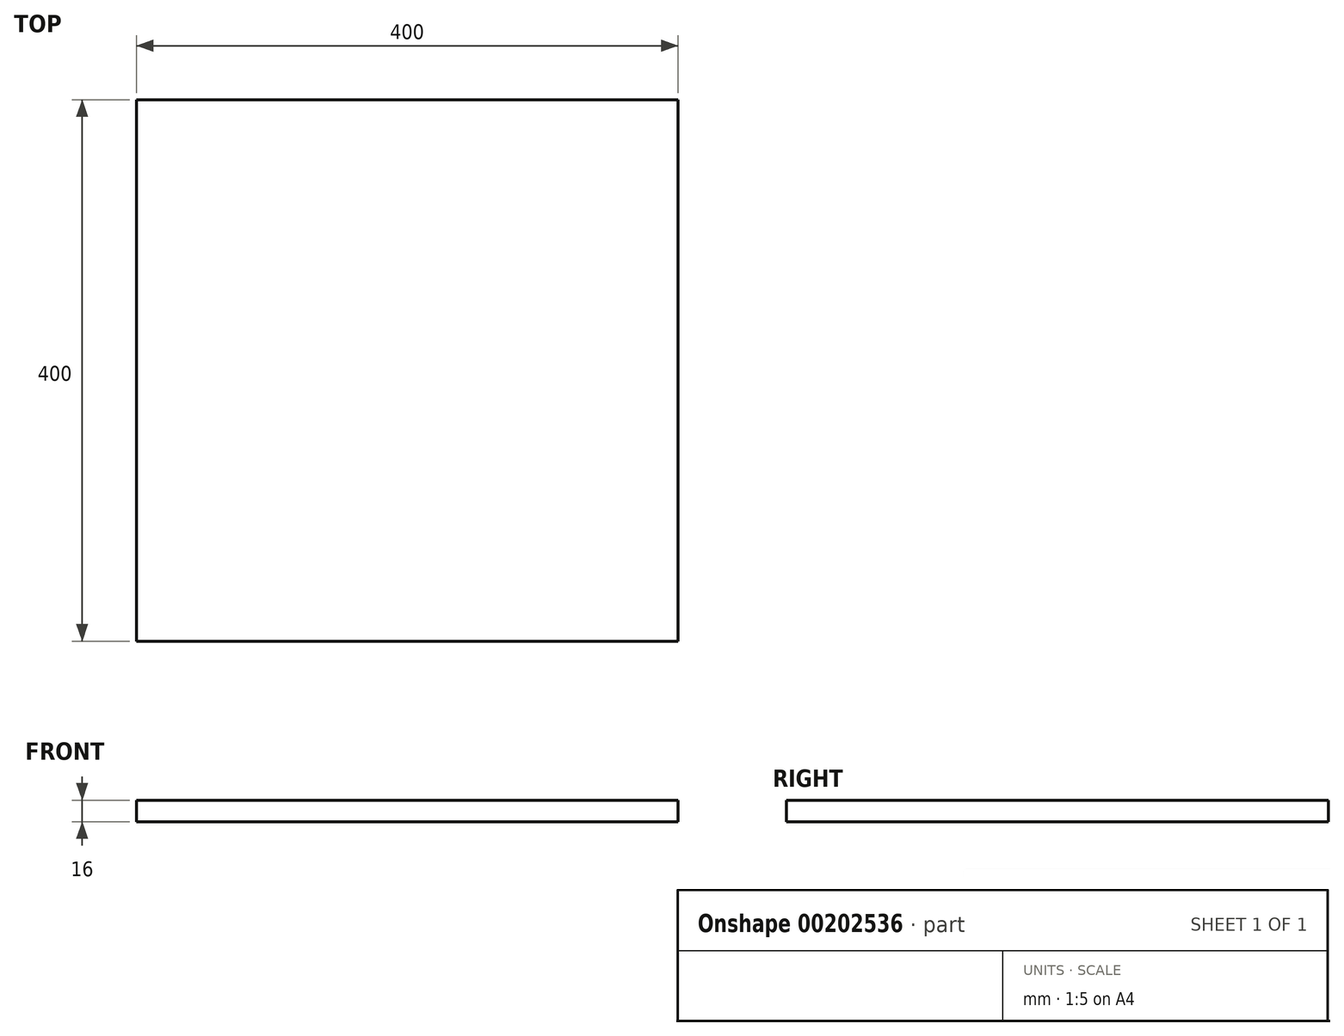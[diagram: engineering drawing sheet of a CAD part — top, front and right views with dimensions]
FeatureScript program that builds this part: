
annotation { "Feature Type Name" : "Feature", "Feature Type Description" : "" }
export const myFeature = defineFeature(function(context is Context, id is Id, definition is map)
    precondition{}
    {
        {
            var Q0;
            Q0=qCreatedBy(makeId("Top.planeOp"),FACE);
            var sketch = newSketch(context, id + "F0", { "sketchPlane" : qUnion([Q0])});
            skLineSegment(sketch, "E0.bottom", {"start": v(-276.3, -87.4) * mm, "end": v(123.7, -87.4) * mm});
            skLineSegment(sketch, "E0.top", {"start": v(-276.3, 312.6) * mm, "end": v(123.7, 312.6) * mm});
            skLineSegment(sketch, "E0.left", {"start": v(-276.3, -87.4) * mm, "end": v(-276.3, 312.6) * mm});
            skLineSegment(sketch, "E0.right", {"start": v(123.7, -87.4) * mm, "end": v(123.7, 312.6) * mm});
            skSolve(sketch);
        }
        {
            var Q0;
            Q0=makeQuery(id+"F0.imprint","IMPRINT",FACE,{"disambiguationData":[TD([[makeQuery(id+"F0.imprint","IMPRINT",EDGE,{"derivedFrom":sQuery(id+"F0.wireOp",EDGE,"E0.bottom")}),1.0]])]});
            extrude(context, id + "F1", {"entities" : qUnion([Q0]), "depth" : 16 * mm});
        }
    });
